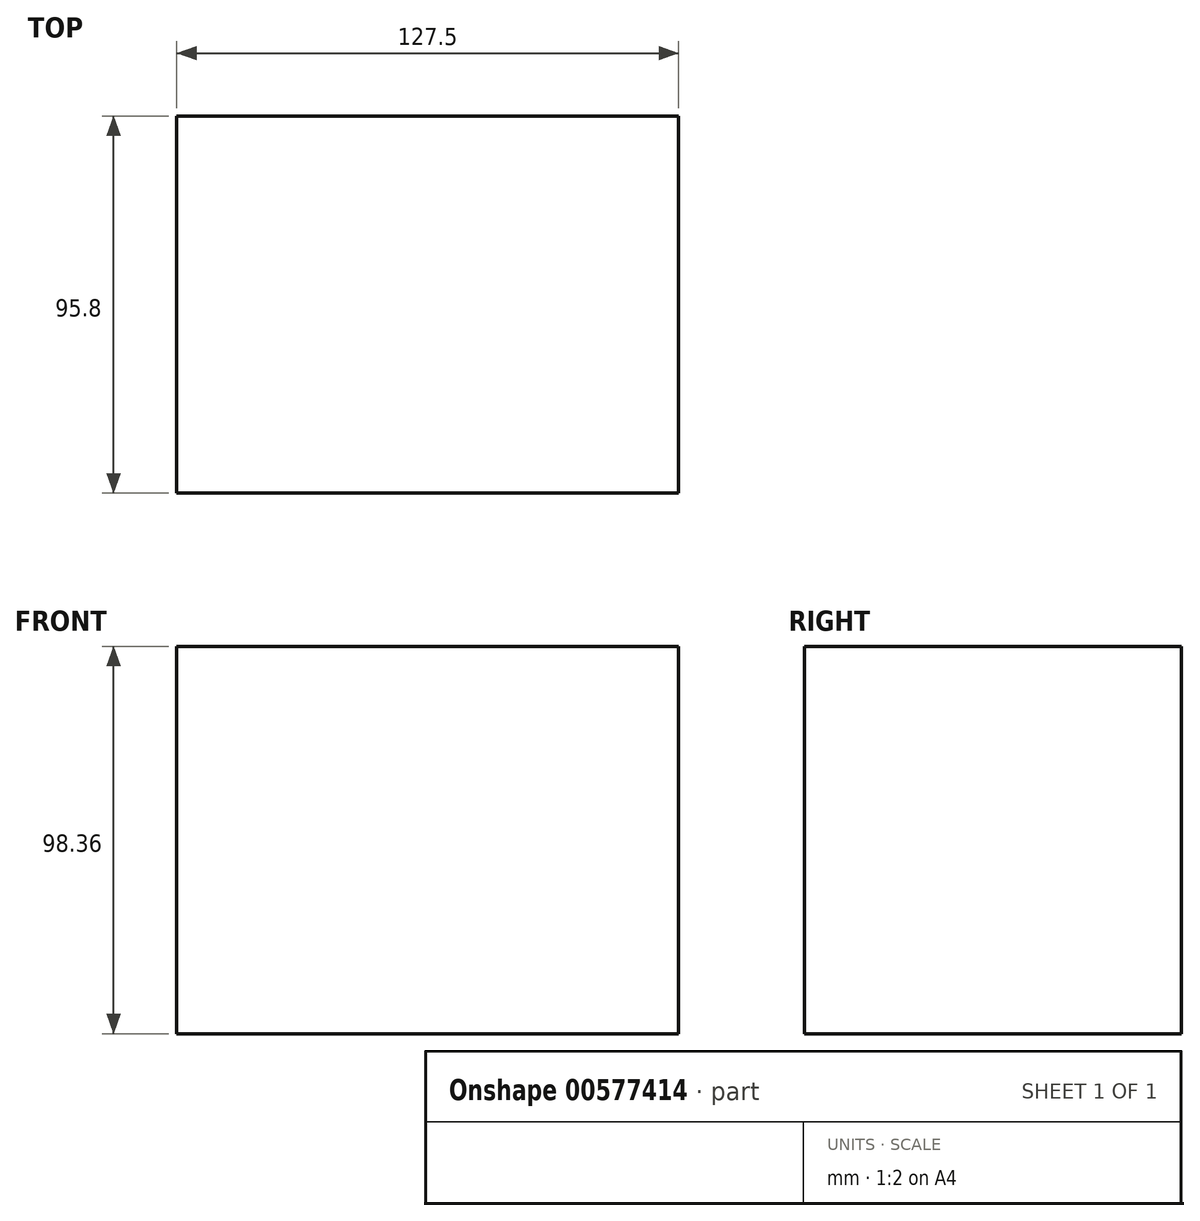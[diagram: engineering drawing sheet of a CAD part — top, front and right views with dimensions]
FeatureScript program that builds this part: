
annotation { "Feature Type Name" : "Feature", "Feature Type Description" : "" }
export const myFeature = defineFeature(function(context is Context, id is Id, definition is map)
    precondition{}
    {
        {
            var Q0;
            Q0=qCreatedBy(makeId("Front.planeOp"),FACE);
            var sketch = newSketch(context, id + "F0", { "sketchPlane" : qUnion([Q0])});
            skLineSegment(sketch, "E0.bottom", {"start": v(-63.75, -49.18) * mm, "end": v(63.75, -49.18) * mm});
            skLineSegment(sketch, "E0.top", {"start": v(-63.75, 49.18) * mm, "end": v(63.75, 49.18) * mm});
            skLineSegment(sketch, "E0.left", {"start": v(-63.75, -49.18) * mm, "end": v(-63.75, 49.18) * mm});
            skLineSegment(sketch, "E0.right", {"start": v(63.75, -49.18) * mm, "end": v(63.75, 49.18) * mm});
            skPoint(sketch, "E0.middle", {"position": v(0, 0) * mm});
            skSolve(sketch);
        }
        {
            var Q0;
            Q0=makeQuery(id+"F0.imprint","IMPRINT",FACE,{"disambiguationData":[TD([[makeQuery(id+"F0.imprint","IMPRINT",EDGE,{"derivedFrom":sQuery(id+"F0.wireOp",EDGE,"E0.bottom")}),1.0]])]});
            extrude(context, id + "F1", {"entities" : qUnion([Q0]), "depth" : 95.8 * mm, "offsetDistance" : 25 * mm});
        }
    });
